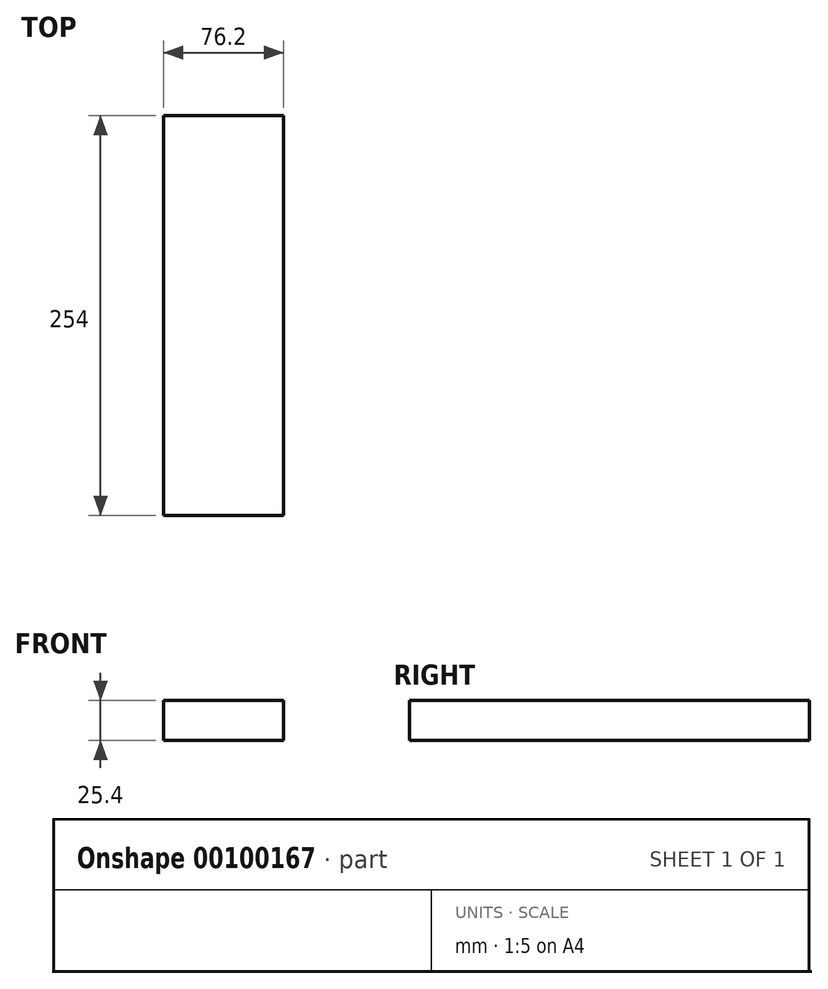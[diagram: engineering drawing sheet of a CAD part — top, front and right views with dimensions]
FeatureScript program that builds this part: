
annotation { "Feature Type Name" : "Feature", "Feature Type Description" : "" }
export const myFeature = defineFeature(function(context is Context, id is Id, definition is map)
    precondition{}
    {
        {
            var Q0;
            Q0=qCreatedBy(makeId("Top.planeOp"),FACE);
            var sketch = newSketch(context, id + "F0", { "sketchPlane" : qUnion([Q0])});
            skLineSegment(sketch, "E0.bottom", {"start": v(38.1, -127) * mm, "end": v(-38.1, -127) * mm});
            skLineSegment(sketch, "E0.top", {"start": v(38.1, 127) * mm, "end": v(-38.1, 127) * mm});
            skLineSegment(sketch, "E0.left", {"start": v(38.1, -127) * mm, "end": v(38.1, 127) * mm});
            skLineSegment(sketch, "E0.right", {"start": v(-38.1, -127) * mm, "end": v(-38.1, 127) * mm});
            skPoint(sketch, "E0.middle", {"position": v(0, 0) * mm});
            skSolve(sketch);
        }
        {
            var Q0;
            Q0 = qSketchRegion(id + "F0", true);
            extrude(context, id + "F1", {"entities" : qUnion([Q0]), "depth" : 25.4 * mm});
        }
    });
